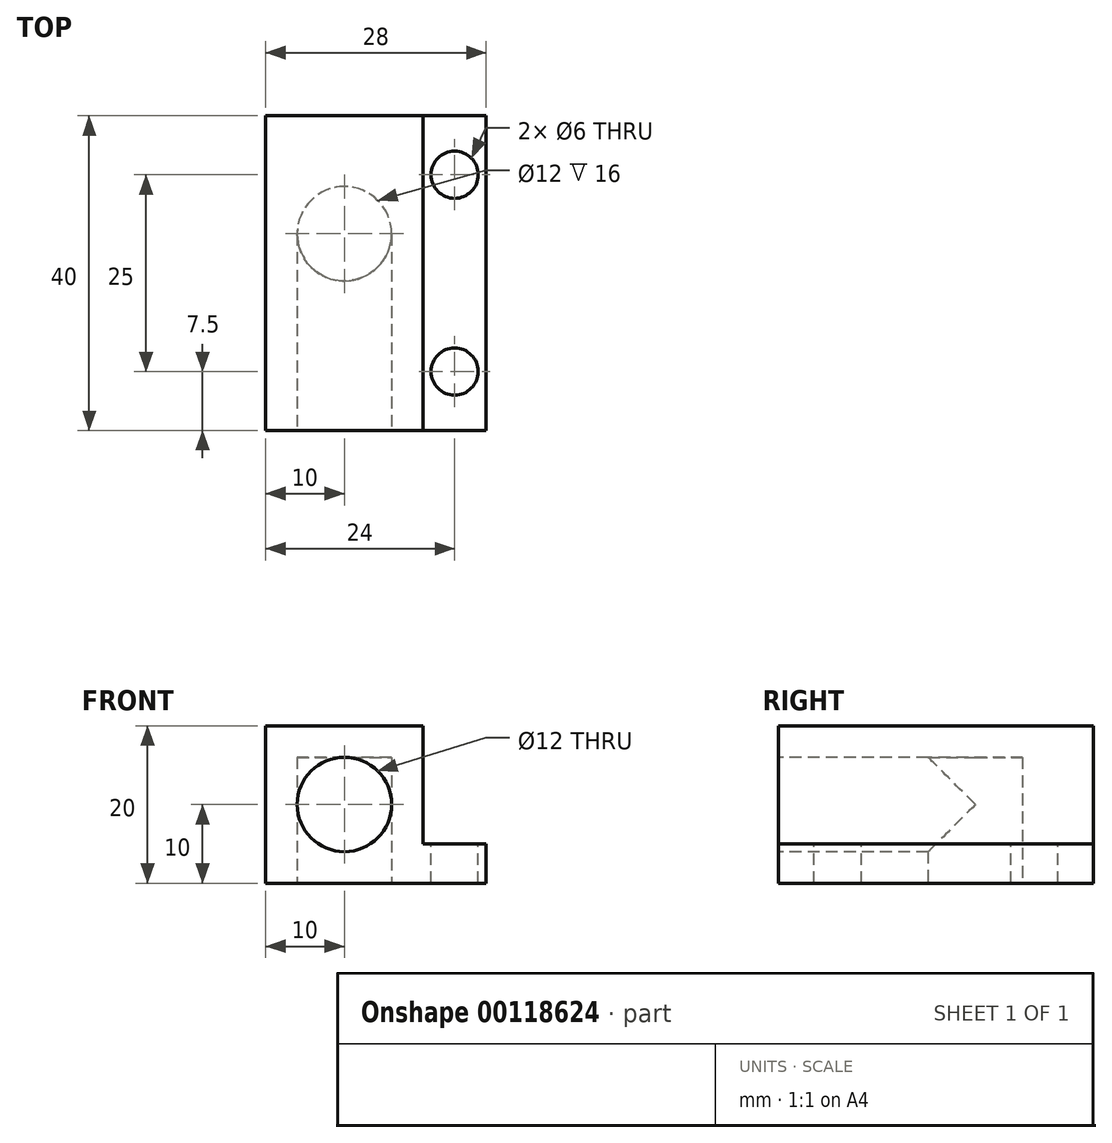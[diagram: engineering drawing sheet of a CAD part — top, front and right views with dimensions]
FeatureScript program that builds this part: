
annotation { "Feature Type Name" : "Feature", "Feature Type Description" : "" }
export const myFeature = defineFeature(function(context is Context, id is Id, definition is map)
    precondition{}
    {
        {
            var Q0;
            Q0=qCreatedBy(makeId("Top.planeOp"),FACE);
            var sketch = newSketch(context, id + "F0", { "sketchPlane" : qUnion([Q0])});
            skLineSegment(sketch, "E0.bottom", {"start": v(0, 0) * mm, "end": v(28, 0) * mm});
            skLineSegment(sketch, "E0.top", {"start": v(0, 40) * mm, "end": v(28, 40) * mm});
            skLineSegment(sketch, "E0.left", {"start": v(0, 0) * mm, "end": v(0, 40) * mm});
            skLineSegment(sketch, "E0.right", {"start": v(28, 0) * mm, "end": v(28, 40) * mm});
            skSolve(sketch);
        }
        {
            var Q0;
            Q0 = qSketchRegion(id + "F0", true);
            extrude(context, id + "F1", {"entities" : qUnion([Q0]), "depth" : 5 * mm});
        }
        {
            var Q0;
            Q0=makeQuery(id+"F1.opExtrude","CAP_FACE",FACE,{"disambiguationData":[OSD([sQuery(id+"F0.wireOp",EDGE,"E0.bottom"),sQuery(id+"F0.wireOp",EDGE,"E0.top"),sQuery(id+"F0.wireOp",EDGE,"E0.left"),sQuery(id+"F0.wireOp",EDGE,"E0.right")])],"isStart":false});
            var sketch = newSketch(context, id + "F2", { "sketchPlane" : qUnion([Q0])});
            skLineSegment(sketch, "E1.bottom", {"start": v(0, 0) * mm, "end": v(20, 0) * mm});
            skLineSegment(sketch, "E1.top", {"start": v(0, 40) * mm, "end": v(20, 40) * mm});
            skLineSegment(sketch, "E1.left", {"start": v(0, 0) * mm, "end": v(0, 40) * mm});
            skLineSegment(sketch, "E1.right", {"start": v(20, 0) * mm, "end": v(20, 40) * mm});
            skSolve(sketch);
        }
        {
            var Q0;
            Q0=makeQuery(id+"F2.imprint","IMPRINT",FACE,{"disambiguationData":[TD([[makeQuery(id+"F2.imprint","IMPRINT",EDGE,{"derivedFrom":sQuery(id+"F2.wireOp",EDGE,"E1.bottom")}),1.0]])]});
            extrude(context, id + "F3", {"entities" : qUnion([Q0]), "operationType" : NewBodyOperationType.ADD, "depth" : 15 * mm});
        }
        {
            var Q0;
            Q0=makeQuery(id+"F3.boolean.opBoolean","MERGE",FACE,{"derivedFrom":[makeQuery(id+"F1.opExtrude","SWEPT_FACE",FACE,{"disambiguationData":[OSD([sQuery(id+"F0.wireOp",EDGE,"E0.bottom")])]}),makeQuery(id+"F3.opExtrude","SWEPT_FACE",FACE,{"disambiguationData":[OSD([sQuery(id+"F2.wireOp",EDGE,"E1.bottom")])]})]});
            var sketch = newSketch(context, id + "F4", { "sketchPlane" : qUnion([Q0])});
            skLineSegment(sketch, "E2", {"start": v(10, 20) * mm, "end": v(10, -3.27) * mm, "construction": true});
            skPoint(sketch, "E3.endSnap0", {"position": v(20, 12.5) * mm});
            skLineSegment(sketch, "E4", {"start": v(1.55, 10) * mm, "end": v(17.95, 10) * mm, "construction": true});
            skCircle(sketch, "E5", {"center": v(10, 10) * mm, "radius": 6 * mm});
            skSolve(sketch);
        }
        {
            var Q0;
            Q0=makeQuery(id+"F1.opExtrude","CAP_FACE",FACE,{"disambiguationData":[OSD([sQuery(id+"F0.wireOp",EDGE,"E0.bottom"),sQuery(id+"F0.wireOp",EDGE,"E0.top"),sQuery(id+"F0.wireOp",EDGE,"E0.left"),sQuery(id+"F0.wireOp",EDGE,"E0.right")])],"isStart":false});
            var sketch = newSketch(context, id + "F5", { "sketchPlane" : qUnion([Q0])});
            skLineSegment(sketch, "E6", {"start": v(24, 40) * mm, "end": v(24, 0) * mm, "construction": true});
            skLineSegment(sketch, "E7", {"start": v(24, 20) * mm, "end": v(24, 32.5) * mm, "construction": true});
            skLineSegment(sketch, "E8", {"start": v(24, 20) * mm, "end": v(46.47, 20) * mm, "construction": true});
            skLineSegment(sketch, "E9.MirrorCS", {"start": v(24, 20) * mm, "end": v(24, 7.5) * mm, "construction": true});
            skSolve(sketch);
        }
        {
            var Q0;
            Q0=sQuery(id+"F5.wireOp",VERTEX,"E7.end");
            var Q1;
            Q1=sQuery(id+"F5.wireOp",VERTEX,"E9.MirrorCS.end");
            var Q2;
            Q2=makeQuery(id+"F1.opExtrude","SWEPT_BODY",BODY,{"disambiguationData":[OSD([sQuery(id+"F0.wireOp",EDGE,"E0.bottom"),sQuery(id+"F0.wireOp",EDGE,"E0.top"),sQuery(id+"F0.wireOp",EDGE,"E0.left"),sQuery(id+"F0.wireOp",EDGE,"E0.right")])]});
            hole(context, id + "F6", {"style" : HoleStyle.SIMPLE, "endStyle" : HoleEndStyle.THROUGH, "holeDiameter" : 6 * mm, "locations" : qUnion([Q0, Q1]), "scope" : qUnion([Q2]), "isTappedThrough" : true});
        }
        {
            var Q0;
            Q0 = qSketchRegion(id + "F4", true);
            extrude(context, id + "F7", {"entities" : qUnion([Q0]), "operationType" : NewBodyOperationType.REMOVE, "oppositeDirection" : true, "depth" : 25 * mm});
        }
        {
            var Q0;
            Q0=makeQuery(id+"F1.opExtrude","CAP_FACE",FACE,{"disambiguationData":[OSD([sQuery(id+"F0.wireOp",EDGE,"E0.bottom"),sQuery(id+"F0.wireOp",EDGE,"E0.top"),sQuery(id+"F0.wireOp",EDGE,"E0.left"),sQuery(id+"F0.wireOp",EDGE,"E0.right")])],"isStart":true});
            var sketch = newSketch(context, id + "F8", { "sketchPlane" : qUnion([Q0])});
            skLineSegment(sketch, "E10", {"start": v(10, -40) * mm, "end": v(10, 0) * mm, "construction": true});
            skLineSegment(sketch, "E11", {"start": v(0, -25) * mm, "end": v(28, -25) * mm, "construction": true});
            skCircle(sketch, "E12", {"center": v(10, -25) * mm, "radius": 6 * mm});
            skSolve(sketch);
        }
        {
            var Q0;
            Q0 = qSketchRegion(id + "F8", true);
            extrude(context, id + "F9", {"entities" : qUnion([Q0]), "operationType" : NewBodyOperationType.REMOVE, "oppositeDirection" : true, "depth" : 16 * mm});
        }
    });
